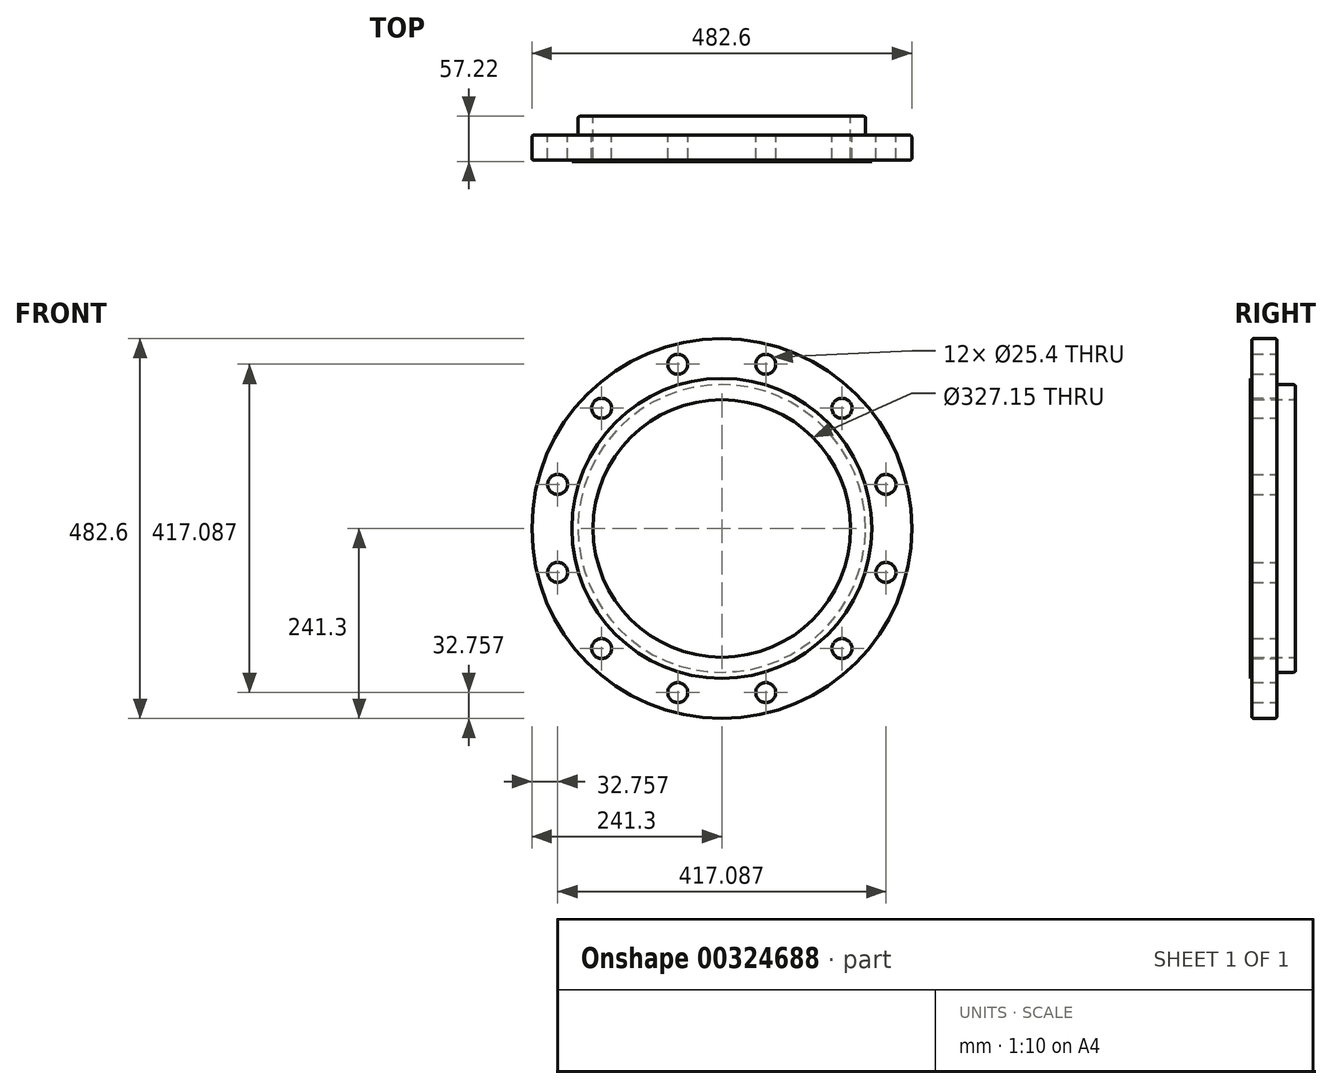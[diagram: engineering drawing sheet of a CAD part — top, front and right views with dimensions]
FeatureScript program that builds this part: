
annotation { "Feature Type Name" : "Feature", "Feature Type Description" : "" }
export const myFeature = defineFeature(function(context is Context, id is Id, definition is map)
    precondition{}
    {
        {
            var Q0;
            Q0=qCreatedBy(makeId("Front.planeOp"),FACE);
            var sketch = newSketch(context, id + "F0", { "sketchPlane" : qUnion([Q0])});
            skCircle(sketch, "E0", {"center": v(0, 0) * mm, "radius": 241.3 * mm});
            skCircle(sketch, "E1", {"center": v(0, 0) * mm, "radius": 163.58 * mm});
            skCircle(sketch, "E2", {"center": v(55.88, 208.54) * mm, "radius": 12.7 * mm});
            skCircle(sketch, "E3.1.0", {"center": v(-55.88, 208.54) * mm, "radius": 12.7 * mm});
            skCircle(sketch, "E3.2.0", {"center": v(-152.66, 152.66) * mm, "radius": 12.7 * mm});
            skCircle(sketch, "E3.3.0", {"center": v(-208.54, 55.88) * mm, "radius": 12.7 * mm});
            skCircle(sketch, "E3.4.0", {"center": v(-208.54, -55.88) * mm, "radius": 12.7 * mm});
            skCircle(sketch, "E3.5.0", {"center": v(-152.66, -152.66) * mm, "radius": 12.7 * mm});
            skCircle(sketch, "E3.6.0", {"center": v(-55.88, -208.54) * mm, "radius": 12.7 * mm});
            skCircle(sketch, "E3.7.0", {"center": v(55.88, -208.54) * mm, "radius": 12.7 * mm});
            skCircle(sketch, "E3.8.0", {"center": v(152.66, -152.66) * mm, "radius": 12.7 * mm});
            skCircle(sketch, "E3.9.0", {"center": v(208.54, -55.88) * mm, "radius": 12.7 * mm});
            skCircle(sketch, "E3.10.0", {"center": v(208.54, 55.88) * mm, "radius": 12.7 * mm});
            skCircle(sketch, "E3.11.0", {"center": v(152.66, 152.66) * mm, "radius": 12.7 * mm});
            skSolve(sketch);
        }
        {
            var Q0;
            Q0=makeQuery(id+"F0.imprint","IMPRINT",FACE,{"disambiguationData":[TD([[makeQuery(id+"F0.imprint","IMPRINT",EDGE,{"derivedFrom":sQuery(id+"F0.wireOp",EDGE,"E0")}),1.0]])]});
            extrude(context, id + "F1", {"entities" : qUnion([Q0]), "depth" : 31.75 * mm});
        }
        {
            var Q0;
            Q0=makeQuery(id+"F1.opExtrude","CAP_FACE",FACE,{"disambiguationData":[OSD([sQuery(id+"F0.wireOp",EDGE,"E0"),sQuery(id+"F0.wireOp",EDGE,"E1"),sQuery(id+"F0.wireOp",EDGE,"E2"),sQuery(id+"F0.wireOp",EDGE,"E3.1.0"),sQuery(id+"F0.wireOp",EDGE,"E3.2.0"),sQuery(id+"F0.wireOp",EDGE,"E3.3.0"),sQuery(id+"F0.wireOp",EDGE,"E3.4.0"),sQuery(id+"F0.wireOp",EDGE,"E3.5.0"),sQuery(id+"F0.wireOp",EDGE,"E3.6.0"),sQuery(id+"F0.wireOp",EDGE,"E3.7.0"),sQuery(id+"F0.wireOp",EDGE,"E3.8.0"),sQuery(id+"F0.wireOp",EDGE,"E3.9.0"),sQuery(id+"F0.wireOp",EDGE,"E3.10.0"),sQuery(id+"F0.wireOp",EDGE,"E3.11.0")])],"isStart":false});
            var sketch = newSketch(context, id + "F2", { "sketchPlane" : qUnion([Q0])});
            skCircle(sketch, "E4", {"center": v(0, 0) * mm, "radius": 190.5 * mm});
            skCircle(sketch, "E5", {"center": v(0, 0) * mm, "radius": 163.58 * mm});
            skSolve(sketch);
        }
        {
            var Q0;
            Q0=makeQuery(id+"F2.imprint","IMPRINT",FACE,{"disambiguationData":[TD([[makeQuery(id+"F2.imprint","IMPRINT",EDGE,{"derivedFrom":sQuery(id+"F2.wireOp",EDGE,"E4")}),1.0]])]});
            extrude(context, id + "F3", {"entities" : qUnion([Q0]), "operationType" : NewBodyOperationType.ADD, "depth" : 1.59 * mm});
        }
        {
            var Q0;
            Q0=makeQuery(id+"F1.opExtrude","CAP_FACE",FACE,{"disambiguationData":[OSD([sQuery(id+"F0.wireOp",EDGE,"E0"),sQuery(id+"F0.wireOp",EDGE,"E1"),sQuery(id+"F0.wireOp",EDGE,"E2"),sQuery(id+"F0.wireOp",EDGE,"E3.1.0"),sQuery(id+"F0.wireOp",EDGE,"E3.2.0"),sQuery(id+"F0.wireOp",EDGE,"E3.3.0"),sQuery(id+"F0.wireOp",EDGE,"E3.4.0"),sQuery(id+"F0.wireOp",EDGE,"E3.5.0"),sQuery(id+"F0.wireOp",EDGE,"E3.6.0"),sQuery(id+"F0.wireOp",EDGE,"E3.7.0"),sQuery(id+"F0.wireOp",EDGE,"E3.8.0"),sQuery(id+"F0.wireOp",EDGE,"E3.9.0"),sQuery(id+"F0.wireOp",EDGE,"E3.10.0"),sQuery(id+"F0.wireOp",EDGE,"E3.11.0")])],"isStart":true});
            var sketch = newSketch(context, id + "F4", { "sketchPlane" : qUnion([Q0])});
            skCircle(sketch, "E6", {"center": v(0, 0) * mm, "radius": 182.63 * mm});
            skCircle(sketch, "E7", {"center": v(0, 0) * mm, "radius": 163.58 * mm});
            skSolve(sketch);
        }
        {
            var Q0;
            Q0 = qSketchRegion(id + "F4", true);
            extrude(context, id + "F5", {"entities" : qUnion([Q0]), "operationType" : NewBodyOperationType.ADD, "depth" : 23.88 * mm});
        }
        {
            var Q0;
            Q0=makeQuery(id+"F5.opExtrude","CAP_EDGE",EDGE,{"disambiguationData":[OSD([sQuery(id+"F4.wireOp",EDGE,"E7")])],"isStart":false});
            var Q1;
            Q1=makeQuery(id+"F5.opExtrude","CAP_EDGE",EDGE,{"disambiguationData":[OSD([sQuery(id+"F4.wireOp",EDGE,"E6")])],"isStart":false});
            var Q2;
            Q2=makeQuery(id+"F1.opExtrude","CAP_EDGE",EDGE,{"disambiguationData":[OSD([sQuery(id+"F0.wireOp",EDGE,"E0")])],"isStart":true});
            var Q3;
            Q3=makeQuery(id+"F1.opExtrude","CAP_EDGE",EDGE,{"disambiguationData":[OSD([sQuery(id+"F0.wireOp",EDGE,"E0")])],"isStart":false});
            var Q4;
            Q4=makeQuery(id+"F3.opExtrude","CAP_EDGE",EDGE,{"disambiguationData":[OSD([sQuery(id+"F2.wireOp",EDGE,"E5")])],"isStart":false});
            fillet(context, id + "F6", {"entities" : qUnion([Q0, Q1, Q2, Q3, Q4]), "radius" : 2.54 * mm, "tangentPropagation" : true, "allowEdgeOverflow" : false});
        }
    });
